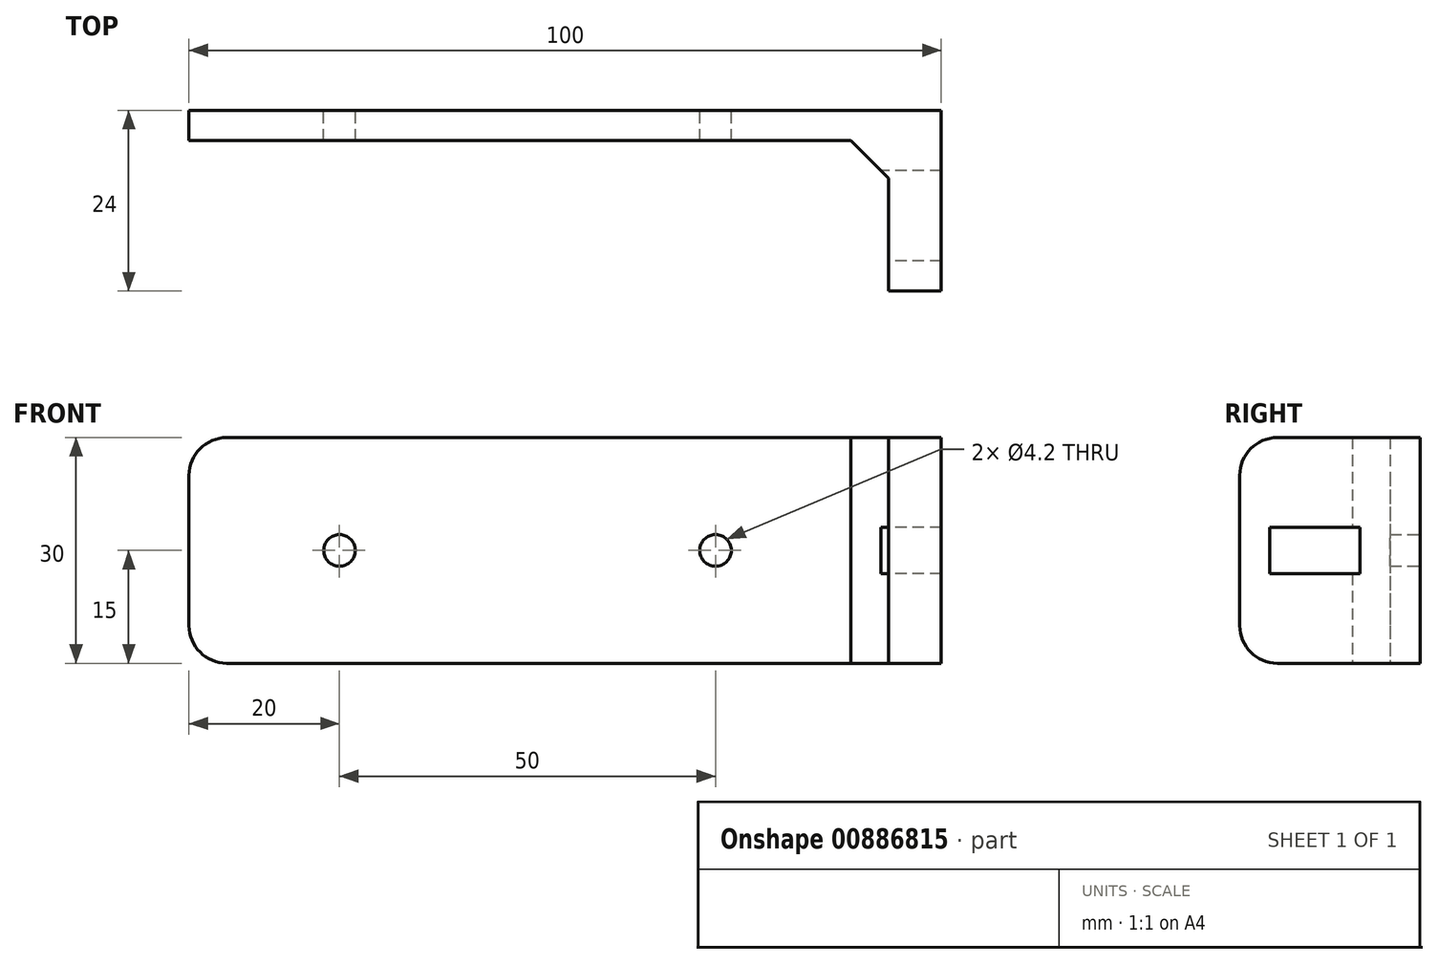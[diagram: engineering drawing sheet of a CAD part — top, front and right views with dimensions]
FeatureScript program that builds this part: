
annotation { "Feature Type Name" : "Feature", "Feature Type Description" : "" }
export const myFeature = defineFeature(function(context is Context, id is Id, definition is map)
    precondition{}
    {
        {
            var Q0;
            Q0=qCreatedBy(makeId("Front.planeOp"),FACE);
            var sketch = newSketch(context, id + "F0", { "sketchPlane" : qUnion([Q0])});
            skCircle(sketch, "E0", {"center": v(-25, 0) * mm, "radius": 2.1 * mm});
            skCircle(sketch, "E1", {"center": v(25, 0) * mm, "radius": 2.1 * mm});
            skLineSegment(sketch, "E2.bottom", {"start": v(-40, 15) * mm, "end": v(55, 15) * mm});
            skLineSegment(sketch, "E2.top", {"start": v(-40, -15) * mm, "end": v(55, -15) * mm});
            skLineSegment(sketch, "E2.left", {"start": v(-45, 10) * mm, "end": v(-45, -10) * mm});
            skLineSegment(sketch, "E2.right", {"start": v(55, 15) * mm, "end": v(55, -15) * mm});
            skPoint(sketch, "E3.visualSharp", {"position": v(-45, 15) * mm});
            skArc(sketch, "E3.filletArc", {"start": v(-40, 15) * mm, "mid": v(-43.54, 13.54) * mm, "end": v(-45, 10) * mm});
            skPoint(sketch, "E4.visualSharp", {"position": v(-45, -15) * mm});
            skArc(sketch, "E4.filletArc", {"start": v(-45, -10) * mm, "mid": v(-43.54, -13.54) * mm, "end": v(-40, -15) * mm});
            skSolve(sketch);
        }
        {
            var Q0;
            Q0=makeQuery(id+"F0.imprint","IMPRINT",FACE,{"disambiguationData":[TD([[makeQuery(id+"F0.imprint","IMPRINT",EDGE,{"derivedFrom":sQuery(id+"F0.wireOp",EDGE,"E0")}),-1.0]])]});
            extrude(context, id + "F1", {"entities" : qUnion([Q0]), "depth" : 4 * mm, "offsetDistance" : 25 * mm});
        }
        {
            var Q0;
            Q0=makeQuery(id+"F1.opExtrude","CAP_FACE",FACE,{"disambiguationData":[OSD([sQuery(id+"F0.wireOp",EDGE,"E0"),sQuery(id+"F0.wireOp",EDGE,"E1"),sQuery(id+"F0.wireOp",EDGE,"E2.bottom"),sQuery(id+"F0.wireOp",EDGE,"E2.top"),sQuery(id+"F0.wireOp",EDGE,"E2.left"),sQuery(id+"F0.wireOp",EDGE,"E2.right"),sQuery(id+"F0.wireOp",EDGE,"E3.filletArc"),sQuery(id+"F0.wireOp",EDGE,"E4.filletArc")])],"isStart":false});
            var sketch = newSketch(context, id + "F2", { "sketchPlane" : qUnion([Q0])});
            skLineSegment(sketch, "E5.bottom", {"start": v(55, 15) * mm, "end": v(48, 15) * mm});
            skLineSegment(sketch, "E5.top", {"start": v(55, -15) * mm, "end": v(48, -15) * mm});
            skLineSegment(sketch, "E5.left", {"start": v(55, 15) * mm, "end": v(55, -15) * mm});
            skLineSegment(sketch, "E5.right", {"start": v(48, 15) * mm, "end": v(48, -15) * mm});
            skSolve(sketch);
        }
        {
            var Q0;
            Q0=makeQuery(id+"F2.imprint","IMPRINT",FACE,{"disambiguationData":[TD([[makeQuery(id+"F2.imprint","IMPRINT",EDGE,{"derivedFrom":sQuery(id+"F2.wireOp",EDGE,"E5.bottom")}),-1.0]])]});
            extrude(context, id + "F3", {"entities" : qUnion([Q0]), "operationType" : NewBodyOperationType.ADD, "depth" : 20 * mm, "offsetDistance" : 25 * mm});
        }
        {
            var Q0;
            Q0=makeQuery(id+"F3.opExtrude","SWEPT_FACE",FACE,{"disambiguationData":[OSD([sQuery(id+"F2.wireOp",EDGE,"E5.right")])]});
            var sketch = newSketch(context, id + "F4", { "sketchPlane" : qUnion([Q0])});
            skLineSegment(sketch, "E6.bottom", {"start": v(4, 15) * mm, "end": v(24, 15) * mm});
            skLineSegment(sketch, "E6.top", {"start": v(4, -15) * mm, "end": v(24, -15) * mm});
            skLineSegment(sketch, "E6.left", {"start": v(4, 15) * mm, "end": v(4, -15) * mm});
            skLineSegment(sketch, "E6.right", {"start": v(24, 15) * mm, "end": v(24, -15) * mm});
            skLineSegment(sketch, "E7.bottom", {"start": v(20, 3.1) * mm, "end": v(8, 3.1) * mm});
            skLineSegment(sketch, "E7.top", {"start": v(20, -3.1) * mm, "end": v(8, -3.1) * mm});
            skLineSegment(sketch, "E7.left", {"start": v(20, 3.1) * mm, "end": v(20, -3.1) * mm});
            skLineSegment(sketch, "E7.right", {"start": v(8, 3.1) * mm, "end": v(8, -3.1) * mm});
            skPoint(sketch, "E7.middle", {"position": v(14, 0) * mm});
            skSolve(sketch);
        }
        {
            var Q0;
            Q0=makeQuery(id+"F1.opExtrude","CAP_FACE",FACE,{"disambiguationData":[OSD([sQuery(id+"F0.wireOp",EDGE,"E0"),sQuery(id+"F0.wireOp",EDGE,"E1"),sQuery(id+"F0.wireOp",EDGE,"E2.bottom"),sQuery(id+"F0.wireOp",EDGE,"E2.top"),sQuery(id+"F0.wireOp",EDGE,"E2.left"),sQuery(id+"F0.wireOp",EDGE,"E2.right"),sQuery(id+"F0.wireOp",EDGE,"E3.filletArc"),sQuery(id+"F0.wireOp",EDGE,"E4.filletArc")])],"isStart":false});
            var sketch = newSketch(context, id + "F5", { "sketchPlane" : qUnion([Q0])});
            skLineSegment(sketch, "E8.bottom", {"start": v(48, 15) * mm, "end": v(43, 15) * mm});
            skLineSegment(sketch, "E8.top", {"start": v(48, -15) * mm, "end": v(43, -15) * mm});
            skLineSegment(sketch, "E8.left", {"start": v(48, 15) * mm, "end": v(48, -15) * mm});
            skLineSegment(sketch, "E8.right", {"start": v(43, 15) * mm, "end": v(43, -15) * mm});
            skSolve(sketch);
        }
        {
            var Q0;
            Q0 = qSketchRegion(id + "F5", true);
            extrude(context, id + "F6", {"entities" : qUnion([Q0]), "operationType" : NewBodyOperationType.ADD, "depth" : 5 * mm, "offsetDistance" : 25 * mm});
        }
        {
            var Q0;
            Q0=makeQuery(id+"F6.opExtrude","CAP_EDGE",EDGE,{"disambiguationData":[OSD([sQuery(id+"F5.wireOp",EDGE,"E8.right")])],"isStart":false});
            chamfer(context, id + "F7", {"entities" : qUnion([Q0]), "width" : 5 * mm, "tangentPropagation" : true});
        }
        {
            var Q0;
            Q0=makeQuery(id+"F4.imprint","IMPRINT",FACE,{"disambiguationData":[TD([[makeQuery(id+"F4.imprint","IMPRINT",EDGE,{"derivedFrom":sQuery(id+"F4.wireOp",EDGE,"E7.bottom")}),1.0]])]});
            extrude(context, id + "F8", {"entities" : qUnion([Q0]), "operationType" : NewBodyOperationType.REMOVE, "endBound" : BoundingType.SYMMETRIC, "oppositeDirection" : true, "depth" : 21.6 * mm, "offsetDistance" : 25 * mm});
        }
        {
            var Q0;
            Q0=makeQuery(id+"F3.opExtrude","CAP_EDGE",EDGE,{"disambiguationData":[OSD([sQuery(id+"F2.wireOp",EDGE,"E5.bottom")])],"isStart":false});
            var Q1;
            Q1=makeQuery(id+"F3.opExtrude","CAP_EDGE",EDGE,{"disambiguationData":[OSD([sQuery(id+"F2.wireOp",EDGE,"E5.top")])],"isStart":false});
            fillet(context, id + "F9", {"entities" : qUnion([Q0, Q1]), "radius" : 5 * mm, "tangentPropagation" : true, "allowEdgeOverflow" : false});
        }
    });
